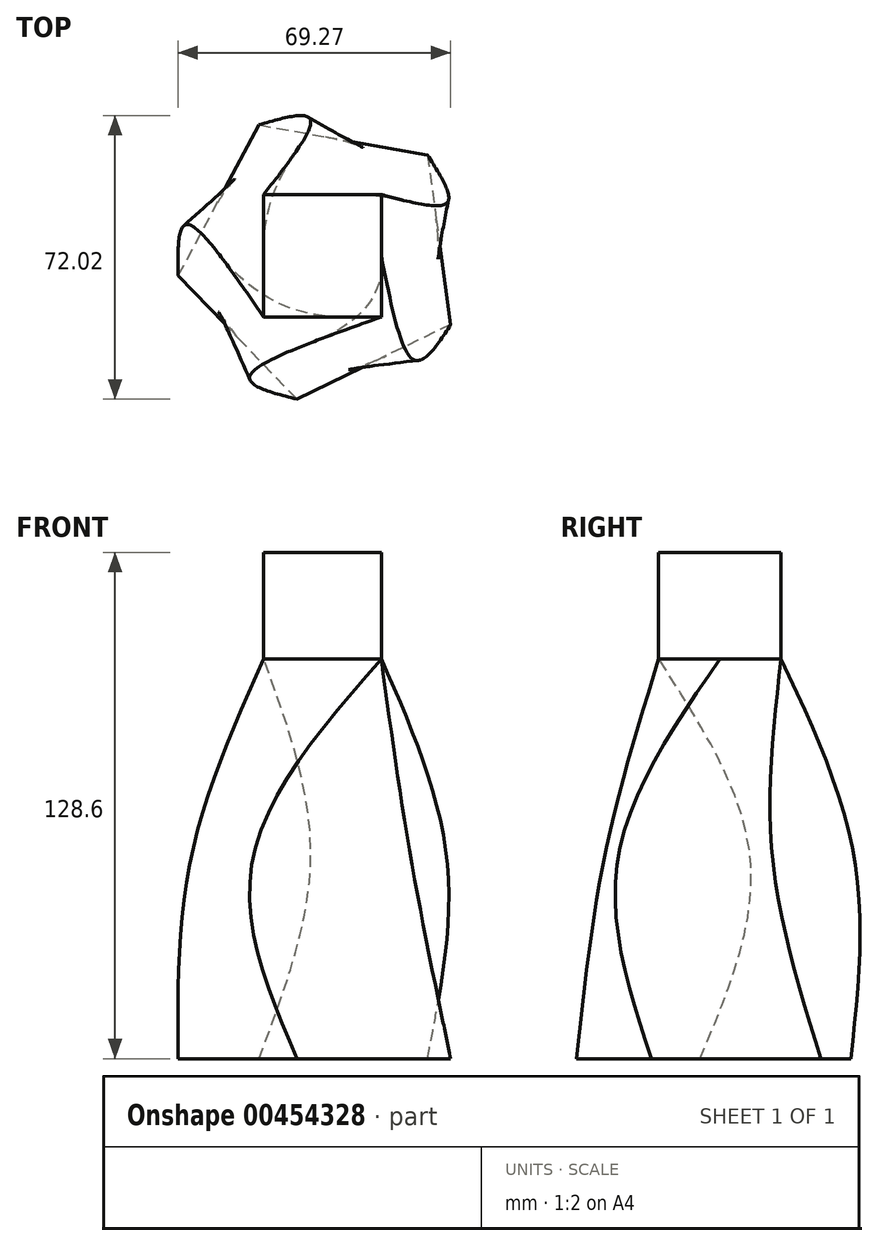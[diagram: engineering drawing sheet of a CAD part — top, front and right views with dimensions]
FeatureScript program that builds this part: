
annotation { "Feature Type Name" : "Feature", "Feature Type Description" : "" }
export const myFeature = defineFeature(function(context is Context, id is Id, definition is map)
    precondition{}
    {
        {
            var Q0;
            Q0=qCreatedBy(makeId("Top.planeOp"),FACE);
            cPlane(context, id + "F0", {"entities" : qUnion([Q0]), "cplaneType" : CPlaneType.OFFSET, "offset" : 50.8 * mm, "oppositeDirection" : true, "width" : 152.4 * mm, "height" : 152.4 * mm});
        }
        {
            var Q0;
            Q0=qCreatedBy(id+"F0.planeOp",FACE);
            var sketch = newSketch(context, id + "F1", { "sketchPlane" : qUnion([Q0])});
            skCircle(sketch, "E0.cCircle", {"center": v(0, 0) * mm, "radius": 27.76 * mm, "construction": true});
            skLineSegment(sketch, "E0.0", {"start": v(-2.97, 34.18) * mm, "end": v(31.59, 13.4) * mm});
            skLineSegment(sketch, "E0.1", {"start": v(31.59, 13.4) * mm, "end": v(22.5, -25.9) * mm});
            skLineSegment(sketch, "E0.2", {"start": v(22.5, -25.9) * mm, "end": v(-17.69, -29.4) * mm});
            skLineSegment(sketch, "E0.3", {"start": v(-17.69, -29.4) * mm, "end": v(-33.43, 7.73) * mm});
            skLineSegment(sketch, "E0.4", {"start": v(-33.43, 7.73) * mm, "end": v(-2.97, 34.18) * mm});
            skPoint(sketch, "E0.0.midPoint", {"position": v(14.3, 23.79) * mm});
            skSolve(sketch);
        }
        {
            var Q0;
            Q0=qCreatedBy(makeId("Top.planeOp"),FACE);
            cPlane(context, id + "F2", {"entities" : qUnion([Q0]), "cplaneType" : CPlaneType.OFFSET, "offset" : 101.6 * mm, "oppositeDirection" : true, "width" : 152.4 * mm, "height" : 152.4 * mm});
        }
        {
            var Q0;
            Q0=qCreatedBy(id+"F2.planeOp",FACE);
            var sketch = newSketch(context, id + "F3", { "sketchPlane" : qUnion([Q0])});
            skCircle(sketch, "E1.cCircle", {"center": v(0, 0) * mm, "radius": 29.9 * mm, "construction": true});
            skLineSegment(sketch, "E1.0", {"start": v(-16.12, 33.26) * mm, "end": v(26.65, 25.61) * mm});
            skLineSegment(sketch, "E1.1", {"start": v(26.65, 25.61) * mm, "end": v(32.6, -17.43) * mm});
            skLineSegment(sketch, "E1.2", {"start": v(32.6, -17.43) * mm, "end": v(-6.5, -36.39) * mm});
            skLineSegment(sketch, "E1.3", {"start": v(-6.5, -36.39) * mm, "end": v(-36.62, -5.05) * mm});
            skLineSegment(sketch, "E1.4", {"start": v(-36.62, -5.05) * mm, "end": v(-16.12, 33.26) * mm});
            skPoint(sketch, "E1.0.midPoint", {"position": v(5.27, 29.44) * mm});
            skSolve(sketch);
        }
        {
            var Q0;
            Q0=qCreatedBy(makeId("Top.planeOp"),FACE);
            var sketch = newSketch(context, id + "F4", { "sketchPlane" : qUnion([Q0])});
            skLineSegment(sketch, "E2.bottom", {"start": v(14.95, -15.56) * mm, "end": v(-14.95, -15.56) * mm});
            skLineSegment(sketch, "E2.top", {"start": v(14.95, 15.56) * mm, "end": v(-14.95, 15.56) * mm});
            skLineSegment(sketch, "E2.left", {"start": v(14.95, -15.56) * mm, "end": v(14.95, 15.56) * mm});
            skLineSegment(sketch, "E2.right", {"start": v(-14.95, -15.56) * mm, "end": v(-14.95, 15.56) * mm});
            skPoint(sketch, "E2.middle", {"position": v(0, 0) * mm});
            skSolve(sketch);
        }
        {
            var Q0;
            Q0=makeQuery(id+"F3.imprint","IMPRINT",FACE,{"disambiguationData":[TD([[makeQuery(id+"F3.imprint","IMPRINT",EDGE,{"derivedFrom":sQuery(id+"F3.wireOp",EDGE,"E1.0")}),-1.0]])]});
            var Q1;
            Q1=makeQuery(id+"F1.imprint","IMPRINT",FACE,{"disambiguationData":[TD([[makeQuery(id+"F1.imprint","IMPRINT",EDGE,{"derivedFrom":sQuery(id+"F1.wireOp",EDGE,"E0.0")}),-1.0]])]});
            var Q2;
            Q2=makeQuery(id+"F4.imprint","IMPRINT",FACE,{"disambiguationData":[TD([[makeQuery(id+"F4.imprint","IMPRINT",EDGE,{"derivedFrom":sQuery(id+"F4.wireOp",EDGE,"E2.bottom")}),-1.0]])]});
            loft(context, id + "F5", {"sheetProfilesArray" : [{ "sheetProfileEntities" : qUnion([Q0]) }, { "sheetProfileEntities" : qUnion([Q1]) }, { "sheetProfileEntities" : qUnion([Q2]) }]});
        }
        {
            var Q0;
            Q0=makeQuery(id+"F5.opLoft","CAP_FACE",FACE,{"disambiguationData":[OSD([makeQuery(id+"F4.imprint","IMPRINT",FACE,{"disambiguationData":[TD([[makeQuery(id+"F4.imprint","IMPRINT",EDGE,{"derivedFrom":sQuery(id+"F4.wireOp",EDGE,"E2.bottom")}),-1.0]])]})])],"isStart":true});
            extrude(context, id + "F6", {"entities" : qUnion([Q0]), "operationType" : NewBodyOperationType.ADD, "depth" : 27 * mm});
        }
        {
            var Q0;
            Q0=makeQuery(id+"F6.opExtrude","SWEPT_FACE",FACE,{"disambiguationData":[OSD([sQuery(id+"F4.wireOp",EDGE,"E2.bottom"),sQuery(id+"F4.wireOp",EDGE,"E2.left"),sQuery(id+"F4.wireOp",EDGE,"E2.right")])]});
            var sketch = newSketch(context, id + "F7", { "sketchPlane" : qUnion([Q0])});
            skCircle(sketch, "E3", {"center": v(0, 14.18) * mm, "radius": 3.24 * mm});
            skSolve(sketch);
        }
        {
            var Q0;
            Q0=sQuery(id+"F7.wireOp",EDGE,"E3");
            extrude(context, id + "F8", {"bodyType" : ToolBodyType.SURFACE, "surfaceEntities" : qUnion([Q0]), "depth" : 15 * mm});
        }
    });
